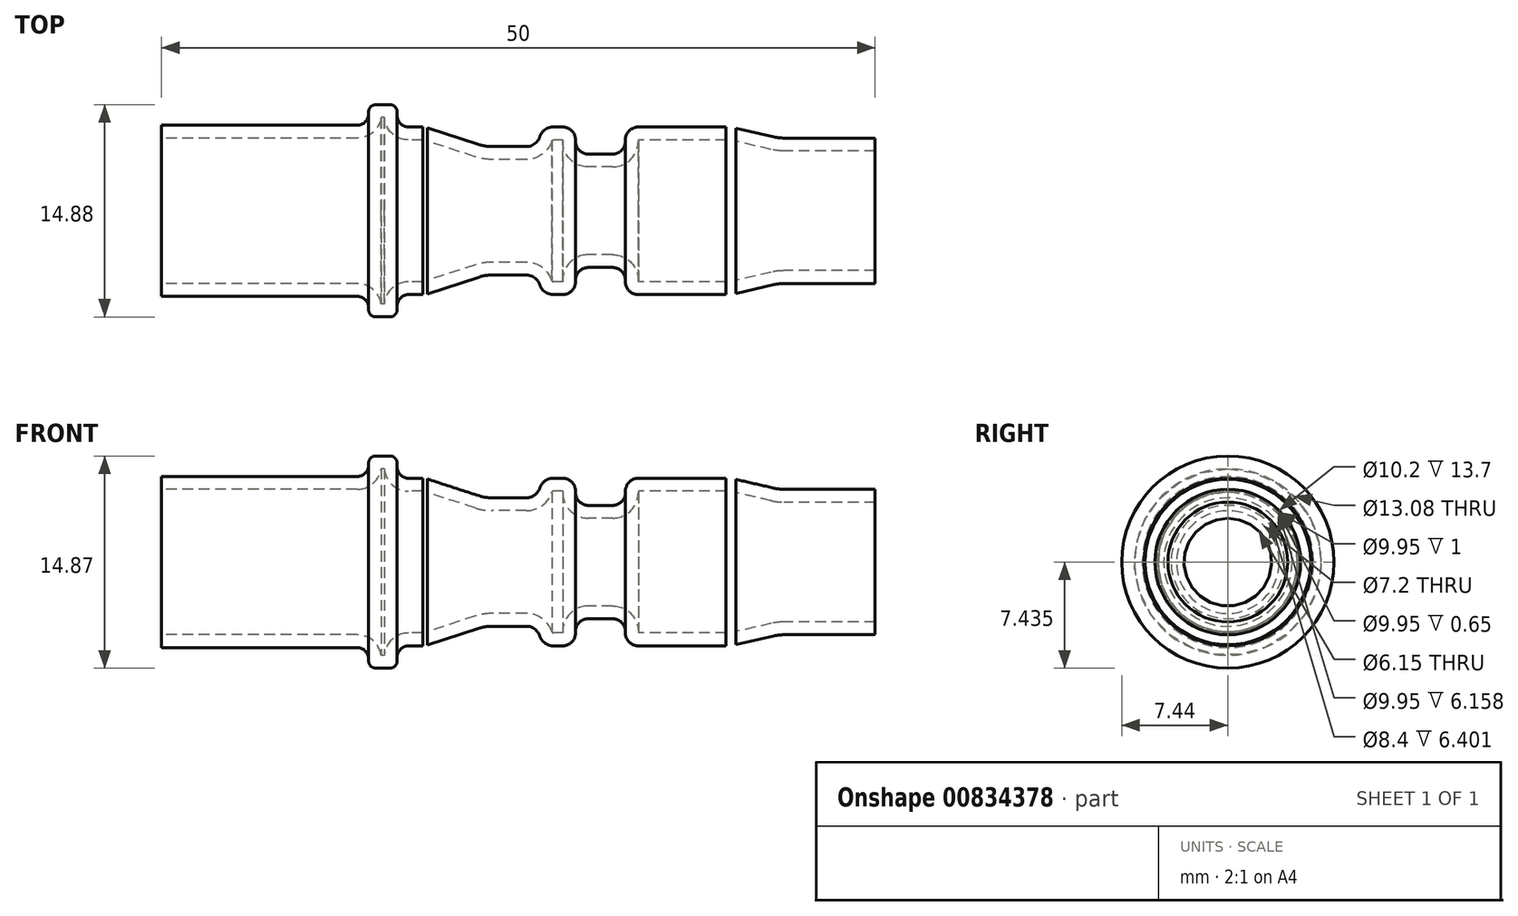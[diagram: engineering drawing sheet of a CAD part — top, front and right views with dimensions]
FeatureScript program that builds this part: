
annotation { "Feature Type Name" : "Feature", "Feature Type Description" : "" }
export const myFeature = defineFeature(function(context is Context, id is Id, definition is map)
    precondition{}
    {
        {
            var Q0;
            Q0=qCreatedBy(makeId("Front.planeOp"),FACE);
            var sketch = newSketch(context, id + "F0", { "sketchPlane" : qUnion([Q0])});
            skLineSegment(sketch, "E0", {"start": v(122.56, 114.97) * mm, "end": v(122.56, 102.97) * mm});
            skLineSegment(sketch, "E1", {"start": v(122.56, 108.97) * mm, "end": v(172.56, 108.97) * mm});
            skLineSegment(sketch, "E2", {"start": v(122.56, 114.97) * mm, "end": v(136.26, 114.97) * mm});
            skArc(sketch, "E3", {"start": v(136.26, 114.97) * mm, "mid": v(136.83, 115.2) * mm, "end": v(137.06, 115.77) * mm});
            skLineSegment(sketch, "E4", {"start": v(137.06, 115.77) * mm, "end": v(137.06, 115.9) * mm});
            skArc(sketch, "E5", {"start": v(137.06, 115.9) * mm, "mid": v(137.2, 116.26) * mm, "end": v(137.56, 116.4) * mm});
            skLineSegment(sketch, "E6", {"start": v(137.56, 116.4) * mm, "end": v(138.56, 116.4) * mm});
            skArc(sketch, "E7", {"start": v(138.56, 116.4) * mm, "mid": v(138.91, 116.26) * mm, "end": v(139.06, 115.9) * mm});
            skLineSegment(sketch, "E8", {"start": v(139.06, 115.9) * mm, "end": v(139.06, 115.64) * mm});
            skArc(sketch, "E9", {"start": v(139.06, 115.64) * mm, "mid": v(139.3, 115.07) * mm, "end": v(139.86, 114.84) * mm});
            skLineSegment(sketch, "E10", {"start": v(139.86, 114.84) * mm, "end": v(140.86, 114.84) * mm});
            skArc(sketch, "E11", {"start": v(140.86, 114.84) * mm, "mid": v(141.02, 114.83) * mm, "end": v(141.17, 114.8) * mm});
            skLineSegment(sketch, "E12", {"start": v(141.17, 114.8) * mm, "end": v(144.8, 113.61) * mm});
            skArc(sketch, "E13", {"start": v(144.8, 113.61) * mm, "mid": v(145.26, 113.5) * mm, "end": v(145.73, 113.47) * mm});
            skLineSegment(sketch, "E14", {"start": v(145.73, 113.47) * mm, "end": v(148.11, 113.47) * mm});
            skArc(sketch, "E15", {"start": v(148.11, 113.47) * mm, "mid": v(148.7, 113.66) * mm, "end": v(149.06, 114.15) * mm});
            skArc(sketch, "E16", {"start": v(149.06, 114.15) * mm, "mid": v(149.42, 114.65) * mm, "end": v(150.01, 114.84) * mm});
            skLineSegment(sketch, "E17", {"start": v(150.01, 114.84) * mm, "end": v(150.66, 114.84) * mm});
            skArc(sketch, "E18", {"start": v(150.66, 114.84) * mm, "mid": v(151.3, 114.58) * mm, "end": v(151.56, 113.94) * mm});
            skLineSegment(sketch, "E19", {"start": v(151.56, 113.94) * mm, "end": v(151.56, 113.84) * mm});
            skArc(sketch, "E20", {"start": v(151.56, 113.84) * mm, "mid": v(151.82, 113.2) * mm, "end": v(152.46, 112.94) * mm});
            skLineSegment(sketch, "E21", {"start": v(152.46, 112.94) * mm, "end": v(154.16, 112.94) * mm});
            skArc(sketch, "E22", {"start": v(154.16, 112.94) * mm, "mid": v(154.8, 113.2) * mm, "end": v(155.06, 113.84) * mm});
            skLineSegment(sketch, "E23", {"start": v(155.06, 113.84) * mm, "end": v(155.06, 113.94) * mm});
            skArc(sketch, "E24", {"start": v(155.06, 113.94) * mm, "mid": v(155.32, 114.58) * mm, "end": v(155.96, 114.84) * mm});
            skLineSegment(sketch, "E25", {"start": v(155.96, 114.84) * mm, "end": v(162.12, 114.84) * mm});
            skArc(sketch, "E26", {"start": v(162.12, 114.84) * mm, "mid": v(162.46, 114.82) * mm, "end": v(162.8, 114.76) * mm});
            skLineSegment(sketch, "E27", {"start": v(162.8, 114.76) * mm, "end": v(165.48, 114.14) * mm});
            skArc(sketch, "E28", {"start": v(165.48, 114.14) * mm, "mid": v(165.82, 114.08) * mm, "end": v(166.16, 114.07) * mm});
            skLineSegment(sketch, "E29", {"start": v(166.16, 114.07) * mm, "end": v(172.56, 114.07) * mm});
            skLineSegment(sketch, "E30", {"start": v(122.56, 114.07) * mm, "end": v(136.26, 114.07) * mm});
            skArc(sketch, "E31", {"start": v(136.26, 114.07) * mm, "mid": v(137.37, 114.47) * mm, "end": v(137.94, 115.5) * mm});
            skLineSegment(sketch, "E32", {"start": v(137.94, 115.5) * mm, "end": v(138.17, 115.5) * mm});
            skArc(sketch, "E33", {"start": v(138.17, 115.5) * mm, "mid": v(138.7, 114.4) * mm, "end": v(139.86, 113.94) * mm});
            skLineSegment(sketch, "E34", {"start": v(139.86, 113.94) * mm, "end": v(140.86, 113.94) * mm});
            skArc(sketch, "E35", {"start": v(140.86, 113.94) * mm, "mid": v(140.88, 113.94) * mm, "end": v(140.9, 113.94) * mm});
            skLineSegment(sketch, "E36", {"start": v(140.9, 113.94) * mm, "end": v(144.52, 112.76) * mm});
            skArc(sketch, "E37", {"start": v(144.52, 112.76) * mm, "mid": v(145.12, 112.61) * mm, "end": v(145.73, 112.57) * mm});
            skLineSegment(sketch, "E38", {"start": v(145.73, 112.57) * mm, "end": v(148.11, 112.57) * mm});
            skArc(sketch, "E39", {"start": v(148.11, 112.57) * mm, "mid": v(149.23, 112.93) * mm, "end": v(149.92, 113.87) * mm});
            skArc(sketch, "E40", {"start": v(149.92, 113.87) * mm, "mid": v(149.95, 113.92) * mm, "end": v(150.01, 113.94) * mm});
            skLineSegment(sketch, "E41", {"start": v(150.01, 113.94) * mm, "end": v(150.66, 113.94) * mm});
            skLineSegment(sketch, "E42", {"start": v(150.66, 113.94) * mm, "end": v(150.66, 113.84) * mm});
            skArc(sketch, "E43", {"start": v(150.66, 113.84) * mm, "mid": v(151.19, 112.57) * mm, "end": v(152.46, 112.04) * mm});
            skLineSegment(sketch, "E44", {"start": v(152.46, 112.04) * mm, "end": v(154.16, 112.04) * mm});
            skArc(sketch, "E45", {"start": v(154.16, 112.04) * mm, "mid": v(155.43, 112.57) * mm, "end": v(155.96, 113.84) * mm});
            skLineSegment(sketch, "E46", {"start": v(155.96, 113.84) * mm, "end": v(155.96, 113.94) * mm});
            skLineSegment(sketch, "E47", {"start": v(155.96, 113.94) * mm, "end": v(162.12, 113.94) * mm});
            skArc(sketch, "E48", {"start": v(162.12, 113.94) * mm, "mid": v(162.36, 113.93) * mm, "end": v(162.6, 113.89) * mm});
            skLineSegment(sketch, "E49", {"start": v(162.6, 113.89) * mm, "end": v(165.28, 113.27) * mm});
            skArc(sketch, "E50", {"start": v(165.28, 113.27) * mm, "mid": v(165.72, 113.2) * mm, "end": v(166.16, 113.17) * mm});
            skLineSegment(sketch, "E51", {"start": v(166.16, 113.17) * mm, "end": v(172.56, 113.17) * mm});
            skLineSegment(sketch, "E52", {"start": v(172.56, 103.87) * mm, "end": v(172.56, 114.07) * mm});
            skLineSegment(sketch, "E53", {"start": v(122.56, 102.97) * mm, "end": v(136.26, 102.97) * mm});
            skArc(sketch, "E54", {"start": v(136.26, 102.97) * mm, "mid": v(136.83, 102.73) * mm, "end": v(137.06, 102.17) * mm});
            skLineSegment(sketch, "E55", {"start": v(137.06, 102.17) * mm, "end": v(137.06, 102.03) * mm});
            skArc(sketch, "E56", {"start": v(137.06, 102.03) * mm, "mid": v(137.2, 101.67) * mm, "end": v(137.56, 101.53) * mm});
            skLineSegment(sketch, "E57", {"start": v(137.56, 101.53) * mm, "end": v(138.56, 101.53) * mm});
            skArc(sketch, "E58", {"start": v(138.56, 101.53) * mm, "mid": v(138.91, 101.67) * mm, "end": v(139.06, 102.03) * mm});
            skLineSegment(sketch, "E59", {"start": v(139.06, 102.03) * mm, "end": v(139.06, 102.3) * mm});
            skArc(sketch, "E60", {"start": v(139.06, 102.3) * mm, "mid": v(139.3, 102.86) * mm, "end": v(139.86, 103.1) * mm});
            skLineSegment(sketch, "E61", {"start": v(139.86, 103.1) * mm, "end": v(140.86, 103.1) * mm});
            skArc(sketch, "E62", {"start": v(140.86, 103.1) * mm, "mid": v(141.02, 103.1) * mm, "end": v(141.17, 103.14) * mm});
            skLineSegment(sketch, "E63", {"start": v(141.17, 103.14) * mm, "end": v(144.8, 104.32) * mm});
            skArc(sketch, "E64", {"start": v(144.8, 104.32) * mm, "mid": v(145.26, 104.43) * mm, "end": v(145.73, 104.47) * mm});
            skLineSegment(sketch, "E65", {"start": v(145.73, 104.47) * mm, "end": v(148.11, 104.47) * mm});
            skArc(sketch, "E66", {"start": v(148.11, 104.47) * mm, "mid": v(148.7, 104.28) * mm, "end": v(149.06, 103.78) * mm});
            skArc(sketch, "E67", {"start": v(149.06, 103.78) * mm, "mid": v(149.42, 103.28) * mm, "end": v(150.01, 103.1) * mm});
            skLineSegment(sketch, "E68", {"start": v(150.01, 103.1) * mm, "end": v(150.66, 103.1) * mm});
            skArc(sketch, "E69", {"start": v(150.66, 103.1) * mm, "mid": v(151.3, 103.35) * mm, "end": v(151.56, 104) * mm});
            skLineSegment(sketch, "E70", {"start": v(151.56, 104) * mm, "end": v(151.56, 104.1) * mm});
            skArc(sketch, "E71", {"start": v(151.56, 104.1) * mm, "mid": v(151.82, 104.73) * mm, "end": v(152.46, 105) * mm});
            skLineSegment(sketch, "E72", {"start": v(152.46, 105) * mm, "end": v(154.16, 105) * mm});
            skArc(sketch, "E73", {"start": v(154.16, 105) * mm, "mid": v(154.8, 104.73) * mm, "end": v(155.06, 104.1) * mm});
            skLineSegment(sketch, "E74", {"start": v(155.06, 104.1) * mm, "end": v(155.06, 104) * mm});
            skArc(sketch, "E75", {"start": v(155.06, 104) * mm, "mid": v(155.32, 103.35) * mm, "end": v(155.96, 103.1) * mm});
            skLineSegment(sketch, "E76", {"start": v(155.96, 103.1) * mm, "end": v(162.12, 103.1) * mm});
            skArc(sketch, "E77", {"start": v(162.12, 103.1) * mm, "mid": v(162.46, 103.1) * mm, "end": v(162.8, 103.17) * mm});
            skLineSegment(sketch, "E78", {"start": v(162.8, 103.17) * mm, "end": v(165.48, 103.79) * mm});
            skArc(sketch, "E79", {"start": v(165.48, 103.79) * mm, "mid": v(165.82, 103.85) * mm, "end": v(166.16, 103.87) * mm});
            skLineSegment(sketch, "E80", {"start": v(166.16, 103.87) * mm, "end": v(172.56, 103.87) * mm});
            skLineSegment(sketch, "E81", {"start": v(122.56, 103.87) * mm, "end": v(136.26, 103.87) * mm});
            skArc(sketch, "E82", {"start": v(136.26, 103.87) * mm, "mid": v(137.37, 103.46) * mm, "end": v(137.94, 102.43) * mm});
            skLineSegment(sketch, "E83", {"start": v(137.94, 102.43) * mm, "end": v(138.17, 102.43) * mm});
            skArc(sketch, "E84", {"start": v(138.17, 102.43) * mm, "mid": v(138.7, 103.54) * mm, "end": v(139.86, 104) * mm});
            skLineSegment(sketch, "E85", {"start": v(139.86, 104) * mm, "end": v(140.86, 104) * mm});
            skArc(sketch, "E86", {"start": v(140.86, 104) * mm, "mid": v(140.88, 104) * mm, "end": v(140.9, 104) * mm});
            skLineSegment(sketch, "E87", {"start": v(140.9, 104) * mm, "end": v(144.52, 105.17) * mm});
            skArc(sketch, "E88", {"start": v(144.52, 105.17) * mm, "mid": v(145.12, 105.32) * mm, "end": v(145.73, 105.37) * mm});
            skLineSegment(sketch, "E89", {"start": v(145.73, 105.37) * mm, "end": v(148.11, 105.37) * mm});
            skArc(sketch, "E90", {"start": v(148.11, 105.37) * mm, "mid": v(149.23, 105) * mm, "end": v(149.92, 104.06) * mm});
            skArc(sketch, "E91", {"start": v(149.92, 104.06) * mm, "mid": v(149.95, 104) * mm, "end": v(150.01, 104) * mm});
            skLineSegment(sketch, "E92", {"start": v(150.01, 104) * mm, "end": v(150.66, 104) * mm});
            skLineSegment(sketch, "E93", {"start": v(150.66, 104) * mm, "end": v(150.66, 104.1) * mm});
            skArc(sketch, "E94", {"start": v(150.66, 104.1) * mm, "mid": v(151.19, 105.36) * mm, "end": v(152.46, 105.9) * mm});
            skLineSegment(sketch, "E95", {"start": v(152.46, 105.9) * mm, "end": v(154.16, 105.9) * mm});
            skArc(sketch, "E96", {"start": v(154.16, 105.9) * mm, "mid": v(155.43, 105.36) * mm, "end": v(155.96, 104.1) * mm});
            skLineSegment(sketch, "E97", {"start": v(155.96, 104.1) * mm, "end": v(155.96, 104) * mm});
            skLineSegment(sketch, "E98", {"start": v(155.96, 104) * mm, "end": v(162.12, 104) * mm});
            skArc(sketch, "E99", {"start": v(162.12, 104) * mm, "mid": v(162.36, 104) * mm, "end": v(162.6, 104.04) * mm});
            skLineSegment(sketch, "E100", {"start": v(162.6, 104.04) * mm, "end": v(165.28, 104.67) * mm});
            skArc(sketch, "E101", {"start": v(165.28, 104.67) * mm, "mid": v(165.72, 104.74) * mm, "end": v(166.16, 104.77) * mm});
            skLineSegment(sketch, "E102", {"start": v(166.16, 104.77) * mm, "end": v(172.56, 104.77) * mm});
            skLineSegment(sketch, "E103", {"start": v(166.16, 114.07) * mm, "end": v(166.16, 103.87) * mm});
            skLineSegment(sketch, "E104", {"start": v(165.48, 114.14) * mm, "end": v(165.48, 103.79) * mm});
            skLineSegment(sketch, "E105", {"start": v(162.12, 114.84) * mm, "end": v(162.12, 103.1) * mm});
            skLineSegment(sketch, "E106", {"start": v(162.8, 114.76) * mm, "end": v(162.8, 103.17) * mm});
            skLineSegment(sketch, "E107", {"start": v(148.11, 113.47) * mm, "end": v(148.11, 104.47) * mm});
            skLineSegment(sketch, "E108", {"start": v(136.26, 114.97) * mm, "end": v(136.26, 102.97) * mm});
            skLineSegment(sketch, "E109", {"start": v(151.56, 113.84) * mm, "end": v(151.56, 104.1) * mm});
            skLineSegment(sketch, "E110", {"start": v(155.06, 113.84) * mm, "end": v(155.06, 104.1) * mm});
            skLineSegment(sketch, "E111", {"start": v(155.96, 114.84) * mm, "end": v(155.96, 103.1) * mm});
            skLineSegment(sketch, "E112", {"start": v(144.8, 113.61) * mm, "end": v(144.8, 104.32) * mm});
            skLineSegment(sketch, "E113", {"start": v(145.73, 113.47) * mm, "end": v(145.73, 104.47) * mm});
            skLineSegment(sketch, "E114", {"start": v(141.17, 114.8) * mm, "end": v(141.17, 103.14) * mm});
            skLineSegment(sketch, "E115", {"start": v(140.86, 114.84) * mm, "end": v(140.86, 103.1) * mm});
            skLineSegment(sketch, "E116", {"start": v(139.86, 114.84) * mm, "end": v(139.86, 103.1) * mm});
            skSolve(sketch);
        }
        {
            var Q0;
            {var subQ0=sQuery(id+"F0.wireOp",EDGE,"E2");Q0=makeQuery(id+"F0.imprint","IMPRINT",FACE,{"disambiguationData":[TD([[makeQuery(id+"F0.imprint","IMPRINT",EDGE,{"derivedFrom":subQ0}),-1.0]])]});}
            var Q1;
            {var subQ4=sQuery(id+"F0.wireOp",EDGE,"E3");Q1=makeQuery(id+"F0.imprint","IMPRINT",FACE,{"disambiguationData":[TD([[makeQuery(id+"F0.imprint","IMPRINT",EDGE,{"derivedFrom":subQ4}),-1.0]])]});}
            var Q2;
            {var subQ0=sQuery(id+"F0.wireOp",EDGE,"E10");Q2=makeQuery(id+"F0.imprint","IMPRINT",FACE,{"disambiguationData":[TD([[makeQuery(id+"F0.imprint","IMPRINT",EDGE,{"derivedFrom":subQ0}),-1.0]])]});}
            var Q3;
            {var subQ1=sQuery(id+"F0.wireOp",EDGE,"E11");Q3=makeQuery(id+"F0.imprint","IMPRINT",FACE,{"disambiguationData":[TD([[makeQuery(id+"F0.imprint","IMPRINT",EDGE,{"derivedFrom":subQ1}),-1.0]])]});}
            var Q4;
            {var subQ1=sQuery(id+"F0.wireOp",EDGE,"E12");Q4=makeQuery(id+"F0.imprint","IMPRINT",FACE,{"disambiguationData":[TD([[makeQuery(id+"F0.imprint","IMPRINT",EDGE,{"derivedFrom":subQ1}),-1.0]])]});}
            var Q5;
            {var subQ0=sQuery(id+"F0.wireOp",EDGE,"E13");Q5=makeQuery(id+"F0.imprint","IMPRINT",FACE,{"disambiguationData":[TD([[makeQuery(id+"F0.imprint","IMPRINT",EDGE,{"derivedFrom":subQ0}),-1.0]])]});}
            var Q6;
            {var subQ6=sQuery(id+"F0.wireOp",EDGE,"E15");Q6=makeQuery(id+"F0.imprint","IMPRINT",FACE,{"disambiguationData":[TD([[makeQuery(id+"F0.imprint","IMPRINT",EDGE,{"derivedFrom":subQ6}),-1.0]])]});}
            var Q7;
            {var subQ0=sQuery(id+"F0.wireOp",EDGE,"E14");Q7=makeQuery(id+"F0.imprint","IMPRINT",FACE,{"disambiguationData":[TD([[makeQuery(id+"F0.imprint","IMPRINT",EDGE,{"derivedFrom":subQ0}),-1.0]])]});}
            var Q8;
            {var subQ5=sQuery(id+"F0.wireOp",EDGE,"E20");Q8=makeQuery(id+"F0.imprint","IMPRINT",FACE,{"disambiguationData":[TD([[makeQuery(id+"F0.imprint","IMPRINT",EDGE,{"derivedFrom":subQ5}),-1.0]])]});}
            var Q9;
            {var subQ1=sQuery(id+"F0.wireOp",EDGE,"E23");Q9=makeQuery(id+"F0.imprint","IMPRINT",FACE,{"disambiguationData":[TD([[makeQuery(id+"F0.imprint","IMPRINT",EDGE,{"derivedFrom":subQ1}),-1.0]])]});}
            var Q10;
            {var subQ0=sQuery(id+"F0.wireOp",EDGE,"E25");Q10=makeQuery(id+"F0.imprint","IMPRINT",FACE,{"disambiguationData":[TD([[makeQuery(id+"F0.imprint","IMPRINT",EDGE,{"derivedFrom":subQ0}),-1.0]])]});}
            var Q11;
            {var subQ1=sQuery(id+"F0.wireOp",EDGE,"E26");Q11=makeQuery(id+"F0.imprint","IMPRINT",FACE,{"disambiguationData":[TD([[makeQuery(id+"F0.imprint","IMPRINT",EDGE,{"derivedFrom":subQ1}),-1.0]])]});}
            var Q12;
            {var subQ1=sQuery(id+"F0.wireOp",EDGE,"E27");Q12=makeQuery(id+"F0.imprint","IMPRINT",FACE,{"disambiguationData":[TD([[makeQuery(id+"F0.imprint","IMPRINT",EDGE,{"derivedFrom":subQ1}),-1.0]])]});}
            var Q13;
            {var subQ0=sQuery(id+"F0.wireOp",EDGE,"E29");Q13=makeQuery(id+"F0.imprint","IMPRINT",FACE,{"disambiguationData":[TD([[makeQuery(id+"F0.imprint","IMPRINT",EDGE,{"derivedFrom":subQ0}),-1.0]])]});}
            var Q14;
            {var subQ0=sQuery(id+"F0.wireOp",EDGE,"E28");Q14=makeQuery(id+"F0.imprint","IMPRINT",FACE,{"disambiguationData":[TD([[makeQuery(id+"F0.imprint","IMPRINT",EDGE,{"derivedFrom":subQ0}),-1.0]])]});}
            var Q15;
            Q15=sQuery(id+"F0.wireOp",EDGE,"E1");
            revolve(context, id + "F1", {"surfaceOperationType" : NewSurfaceOperationType.NEW, "entities" : qUnion([Q0, Q1, Q2, Q3, Q4, Q5, Q6, Q7, Q8, Q9, Q10, Q11, Q12, Q13, Q14]), "axis" : qUnion([Q15]), "revolveType" : RevolveType.FULL});
        }
    });
